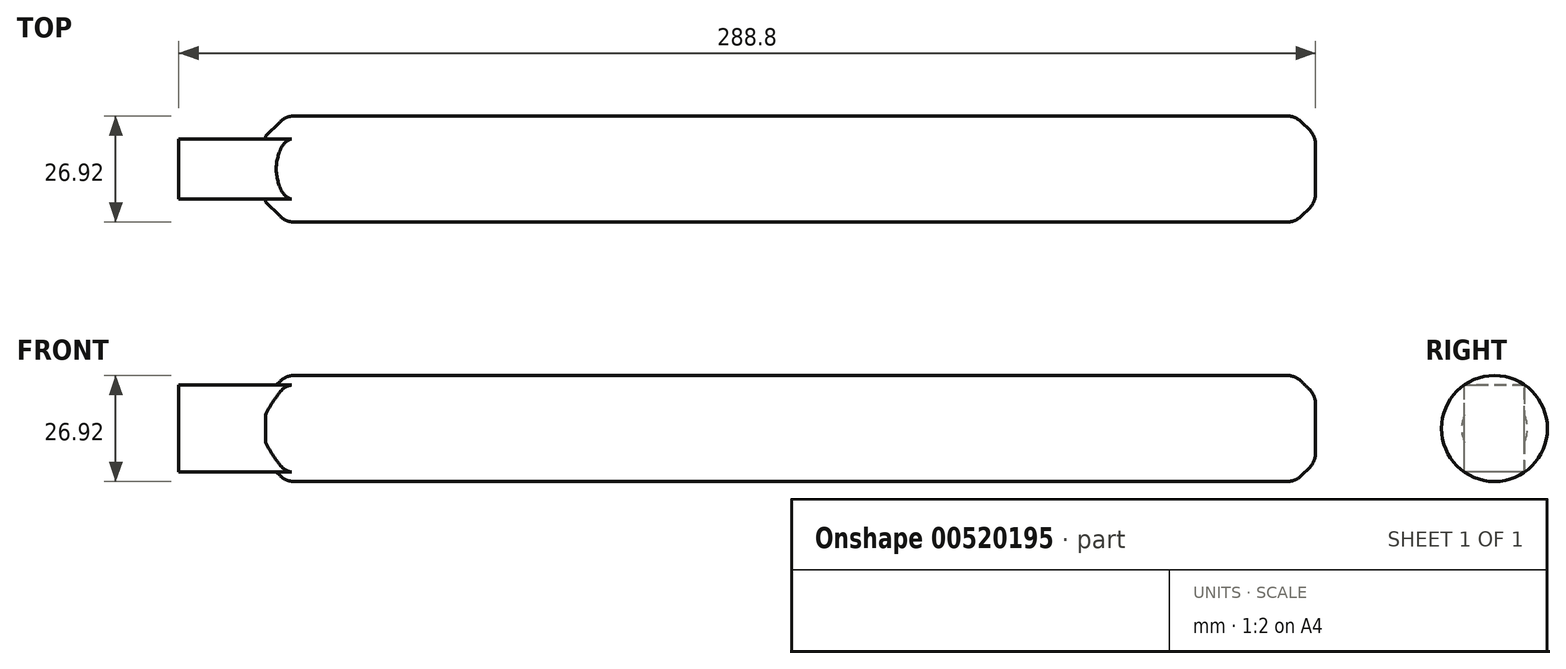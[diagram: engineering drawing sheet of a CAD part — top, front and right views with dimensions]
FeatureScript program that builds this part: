
annotation { "Feature Type Name" : "Feature", "Feature Type Description" : "" }
export const myFeature = defineFeature(function(context is Context, id is Id, definition is map)
    precondition{}
    {
        {
            var Q0;
            Q0=qCreatedBy(makeId("Right.planeOp"),FACE);
            var sketch = newSketch(context, id + "F0", { "sketchPlane" : qUnion([Q0])});
            skLineSegment(sketch, "E0.bottom", {"start": v(7.62, -11.05) * mm, "end": v(-7.62, -11.05) * mm});
            skLineSegment(sketch, "E0.top", {"start": v(7.62, 11.05) * mm, "end": v(-7.62, 11.05) * mm});
            skLineSegment(sketch, "E0.left", {"start": v(7.62, -11.05) * mm, "end": v(7.62, 11.05) * mm});
            skLineSegment(sketch, "E0.right", {"start": v(-7.62, -11.05) * mm, "end": v(-7.62, 11.05) * mm});
            skPoint(sketch, "E0.middle", {"position": v(0, 0) * mm});
            skSolve(sketch);
        }
        {
            var Q0;
            Q0=makeQuery(id+"F0.imprint","IMPRINT",FACE,{"disambiguationData":[TD([[makeQuery(id+"F0.imprint","IMPRINT",EDGE,{"derivedFrom":sQuery(id+"F0.wireOp",EDGE,"E0.bottom")}),-1.0]])]});
            extrude(context, id + "F1", {"entities" : qUnion([Q0]), "depth" : 11.05 * mm, "offsetDistance" : 25.4 * mm});
        }
        {
            var Q0;
            Q0=makeQuery(id+"F1.opExtrude","CAP_FACE",FACE,{"disambiguationData":[OSD([sQuery(id+"F0.wireOp",EDGE,"E0.bottom"),sQuery(id+"F0.wireOp",EDGE,"E0.top"),sQuery(id+"F0.wireOp",EDGE,"E0.left"),sQuery(id+"F0.wireOp",EDGE,"E0.right")])],"isStart":true});
            extrude(context, id + "F2", {"entities" : qUnion([Q0]), "operationType" : NewBodyOperationType.ADD, "depth" : 11.05 * mm, "offsetDistance" : 25.4 * mm});
        }
        {
            var Q0;
            Q0=makeQuery(id+"F1.opExtrude","CAP_FACE",FACE,{"disambiguationData":[OSD([sQuery(id+"F0.wireOp",EDGE,"E0.bottom"),sQuery(id+"F0.wireOp",EDGE,"E0.top"),sQuery(id+"F0.wireOp",EDGE,"E0.left"),sQuery(id+"F0.wireOp",EDGE,"E0.right")])],"isStart":false});
            var sketch = newSketch(context, id + "F3", { "sketchPlane" : qUnion([Q0])});
            skCircle(sketch, "E1", {"center": v(0, 0) * mm, "radius": 13.46 * mm});
            skSolve(sketch);
        }
        {
            var Q0;
            Q0 = qSketchRegion(id + "F3", true);
            extrude(context, id + "F4", {"entities" : qUnion([Q0]), "operationType" : NewBodyOperationType.ADD, "depth" : 266.7 * mm, "offsetDistance" : 25.4 * mm});
        }
        {
            var Q0;
            Q0=makeQuery(id+"F4.opExtrude","CAP_EDGE",EDGE,{"disambiguationData":[OSD([sQuery(id+"F3.wireOp",EDGE,"E1")])],"isStart":false});
            chamfer(context, id + "F5", {"entities" : qUnion([Q0]), "width" : 5.08 * mm, "tangentPropagation" : true});
        }
        {
            var Q0;
            {var subQ0=sQuery(id+"F3.wireOp",EDGE,"E1");Q0=makeQuery(id+"F5.opChamfer","BLEND_EDGE",EDGE,{"blendedFrom":[makeQuery(id+"F4.opExtrude","CAP_EDGE",EDGE,{"disambiguationData":[OSD([subQ0])],"isStart":false}),makeQuery(id+"F4.opExtrude","SWEPT_FACE",FACE,{"disambiguationData":[OSD([subQ0])]})],"blendedInto":[makeQuery(id+"F4.opExtrude","SWEPT_FACE",FACE,{"disambiguationData":[OSD([subQ0])]})]});}
            fillet(context, id + "F6", {"entities" : qUnion([Q0]), "radius" : 5.08 * mm, "tangentPropagation" : true, "allowEdgeOverflow" : false});
        }
        {
            var Q0;
            {var subQ0=sQuery(id+"F3.wireOp",EDGE,"E1");Q0=makeQuery(id+"F5.opChamfer","BLEND_EDGE",EDGE,{"blendedFrom":[makeQuery(id+"F4.opExtrude","CAP_EDGE",EDGE,{"disambiguationData":[OSD([subQ0])],"isStart":false}),makeQuery(id+"F4.opExtrude","CAP_FACE",FACE,{"disambiguationData":[OSD([subQ0])],"isStart":false})],"blendedInto":[makeQuery(id+"F4.opExtrude","CAP_FACE",FACE,{"disambiguationData":[OSD([subQ0])],"isStart":false})]});}
            fillet(context, id + "F7", {"entities" : qUnion([Q0]), "radius" : 5.08 * mm, "tangentPropagation" : true, "allowEdgeOverflow" : false});
        }
        {
            var Q0;
            Q0=makeQuery(id+"F4.opExtrude","CAP_EDGE",EDGE,{"disambiguationData":[OSD([sQuery(id+"F3.wireOp",EDGE,"E1")])],"isStart":true});
            chamfer(context, id + "F8", {"entities" : qUnion([Q0]), "width" : 5.08 * mm, "tangentPropagation" : true});
        }
        {
            var Q0;
            {var subQ0=sQuery(id+"F3.wireOp",EDGE,"E1");Q0=makeQuery(id+"F8.opChamfer","BLEND_EDGE",EDGE,{"blendedFrom":[makeQuery(id+"F4.opExtrude","CAP_EDGE",EDGE,{"disambiguationData":[OSD([subQ0])],"isStart":true}),makeQuery(id+"F4.opExtrude","SWEPT_FACE",FACE,{"disambiguationData":[OSD([subQ0])]})],"blendedInto":[makeQuery(id+"F4.opExtrude","SWEPT_FACE",FACE,{"disambiguationData":[OSD([subQ0])]})]});}
            fillet(context, id + "F9", {"entities" : qUnion([Q0]), "radius" : 5.08 * mm, "tangentPropagation" : true, "allowEdgeOverflow" : false});
        }
    });
